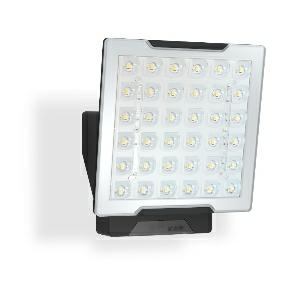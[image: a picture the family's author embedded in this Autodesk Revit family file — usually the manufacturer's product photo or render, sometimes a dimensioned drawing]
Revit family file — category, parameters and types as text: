
# Revit family: xled_pro_square_xl_sl_010003
name_source: partatom
category: Leuchten
revit_build: Autodesk Revit 2016 (Build: 20190508_0715(x64)
units: mm (PartAtom-declared; Revit-internal decimal feet)

## family parameters
Basisbauteil = Fläche
Beim Laden mit Abzugskörper schneiden = Nein
Bemaßung runder Anschluss = Durchmesser verwenden
Gemeinsam genutzt = Nein
Lichtquelle = Nein
Raumberechnungspunkt = Nein
Teiletyp = Normal

## types (1)
- XLED PRO Square XL SL (1 x , 4400 lm, 4000 K)
    Beschreibung = Dimensions (L x W x H): 130 x 178 x 208 mm; Mains power supply: 220 – 240 V / 50 – 60 Hz; Output: 48 W; Luminous flux: 4400 lm; Colour temperature: 4000 K; Colour variation LED: SDCM3; Colour Rendering Index CRI: 80-89; With lamp: Yes, STEINEL LED system; Lamp: LED cannot be replaced; LED life expectancy (max. °C): 50000 h; Drop in luminous flux in accordance with LM80: L70B10; LED cooling system: Passive Thermo Control; With motion detector: No; Photo-cell controller: No; Basic light level function: No; Soft light start: No; Continuous light: selectable, 4h; Impact resistance: IK03; IP-rating: IP54; Protection class: I; Ambient temperature: -20 – 40 °C; Housing material: Aluminium; Cover material: Plastic, transparent; Manufacturer's Warranty: 5 years; PU1, net weight: 1,811 kg; Version: black; PU1, EAN: 4007841010003
    CIE Flux Codes = 53 87 98 99 100
    Color Rendering = 80-89
    Color Temperature = 4000 K
    Frequency = 60 Hz, 50 Hz
    Height = 208 mm
    Hersteller = Steinel
    Lamp Light Flux = 4400 lm
    Lamp count = 1
    Lampe = 1 x
    Length = 130 mm
    Luminous efficacy = 92 lm/W
    ModVariant = Nein
    Modell = 010003
    Mounting Type = Surface mounted
    Number of Poles = 1
    OnlyDefault = Ja
    Power Factor = 1
    Product Name = XLED PRO Square XL SL
    Product group = Sensor-switched indoor light
    ProductGroupID = 30
    Protection Class = Protection class I
    Protection Degree = IP 54
    RlxData = <blob elided: 65465 chars, md5=11631155>
    Scheinlast = 48 VA
    Socket = socket
    Standby Power = 0 W
    System Light Flux = 4400 lm
    System Power = 48 W
    Typenbild = produkt1_010003.jpg
    Typenkommentare = Product without accessories
    URL = http://relux.com
    VarID = ---
    Voltage = 0 V
    Vorgabe-Ansicht = 1800 mm
    Weight = 0.00 kg
    Width = 178 mm

## geometry (parser evidence)
native form markers: Blend x4, Sweep x10
no freeform markers — native parametric forms only
